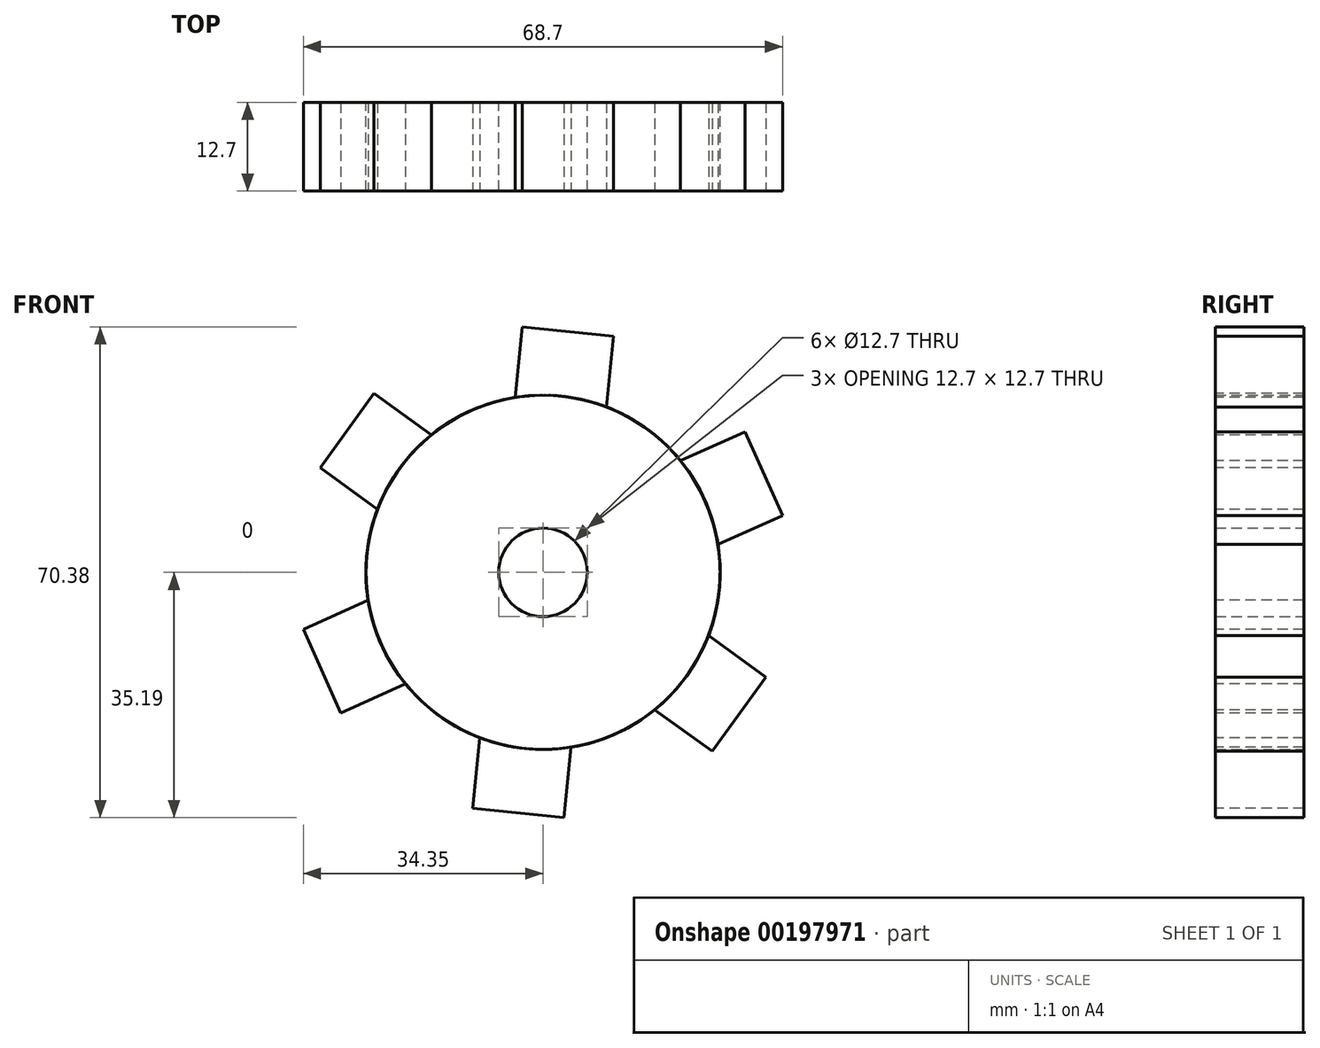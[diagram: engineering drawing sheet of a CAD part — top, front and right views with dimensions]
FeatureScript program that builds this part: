
annotation { "Feature Type Name" : "Feature", "Feature Type Description" : "" }
export const myFeature = defineFeature(function(context is Context, id is Id, definition is map)
    precondition{}
    {
        {
            var Q0;
            Q0=qCreatedBy(makeId("Front.planeOp"),FACE);
            var sketch = newSketch(context, id + "F0", { "sketchPlane" : qUnion([Q0])});
            skCircle(sketch, "E0", {"center": v(0, 0) * mm, "radius": 25.4 * mm});
            skSolve(sketch);
        }
        {
            var Q0;
            Q0=makeQuery(id+"F0.imprint","IMPRINT",FACE,{"disambiguationData":[TD([[makeQuery(id+"F0.imprint","IMPRINT",EDGE,{"derivedFrom":sQuery(id+"F0.wireOp",EDGE,"E0")}),1.0]])]});
            extrude(context, id + "F1", {"entities" : qUnion([Q0]), "endBound" : BoundingType.SYMMETRIC, "depth" : 12.7 * mm});
        }
        {
            var Q0;
            Q0=makeQuery(id+"F1.opExtrude","CAP_FACE",FACE,{"disambiguationData":[OSD([sQuery(id+"F0.wireOp",EDGE,"E0")])],"isStart":false});
            var sketch = newSketch(context, id + "F2", { "sketchPlane" : qUnion([Q0])});
            skLineSegment(sketch, "E1", {"start": v(0, 0) * mm, "end": v(-20.58, 14.9) * mm});
            skLineSegment(sketch, "E2", {"start": v(0, 0) * mm, "end": v(-16.02, 19.71) * mm});
            skLineSegment(sketch, "E3", {"start": v(0, 0) * mm, "end": v(-23.73, 9.06) * mm});
            skLineSegment(sketch, "E4", {"start": v(-23.73, 9.06) * mm, "end": v(-16.02, 19.71) * mm});
            skLineSegment(sketch, "E5.0", {"start": v(-31.96, 15.02) * mm, "end": v(-24.25, 25.67) * mm});
            skLineSegment(sketch, "E6", {"start": v(-31.96, 15.02) * mm, "end": v(-23.73, 9.06) * mm});
            skLineSegment(sketch, "E7", {"start": v(-24.25, 25.67) * mm, "end": v(-16.02, 19.71) * mm});
            skSolve(sketch);
        }
        {
            var Q0;
            Q0 = qSketchRegion(id + "F2", true);
            extrude(context, id + "F3", {"entities" : qUnion([Q0]), "operationType" : NewBodyOperationType.ADD, "oppositeDirection" : true, "depth" : 12.7 * mm});
        }
        {
            var Q0;
            Q0=qCreatedBy(makeId("Top.planeOp"),FACE);
            var sketch = newSketch(context, id + "F4", { "sketchPlane" : qUnion([Q0])});
            skLineSegment(sketch, "E8", {"start": v(0, 0) * mm, "end": v(0, 56.19) * mm});
            skSolve(sketch);
        }
        {
            var Q0;
            Q0=makeQuery(id+"F1.opExtrude","SWEPT_BODY",BODY,{"disambiguationData":[OSD([sQuery(id+"F0.wireOp",EDGE,"E0")])]});
            var Q1;
            Q1=sQuery(id+"F4.wireOp",EDGE,"E8");
            circularPattern(context, id + "F5", {"entities" : qUnion([Q0]), "axis" : qUnion([Q1]), "angle" : 360 * degree, "instanceCount" : 6, "equalSpace" : true});
        }
        {
            var Q0;
            Q0=makeQuery(id+"F5.opPattern","COPY",FACE,{"derivedFrom":makeQuery(id+"F3.boolean.opBoolean","MERGE",FACE,{"derivedFrom":[makeQuery(id+"F1.opExtrude","CAP_FACE",FACE,{"disambiguationData":[OSD([sQuery(id+"F0.wireOp",EDGE,"E0")])],"isStart":true}),makeQuery(id+"F3.opExtrude","CAP_FACE",FACE,{"disambiguationData":[OSD([sQuery(id+"F2.wireOp",EDGE,"E2"),sQuery(id+"F2.wireOp",EDGE,"E3"),sQuery(id+"F2.wireOp",EDGE,"E5.0"),sQuery(id+"F2.wireOp",EDGE,"E6"),sQuery(id+"F2.wireOp",EDGE,"E7")])],"isStart":false})]}),"instanceName":"4"});
            var sketch = newSketch(context, id + "F6", { "sketchPlane" : qUnion([Q0])});
            skCircle(sketch, "E9", {"center": v(0, 0) * mm, "radius": 6.35 * mm});
            skSolve(sketch);
        }
        {
            var Q0;
            Q0=makeQuery(id+"F6.imprint","IMPRINT",FACE,{"disambiguationData":[TD([[makeQuery(id+"F6.imprint","IMPRINT",EDGE,{"derivedFrom":sQuery(id+"F6.wireOp",EDGE,"E9")}),1.0]])]});
            extrude(context, id + "F7", {"entities" : qUnion([Q0]), "operationType" : NewBodyOperationType.REMOVE, "endBound" : BoundingType.THROUGH_ALL, "oppositeDirection" : true, "depth" : 25.4 * mm});
        }
    });
